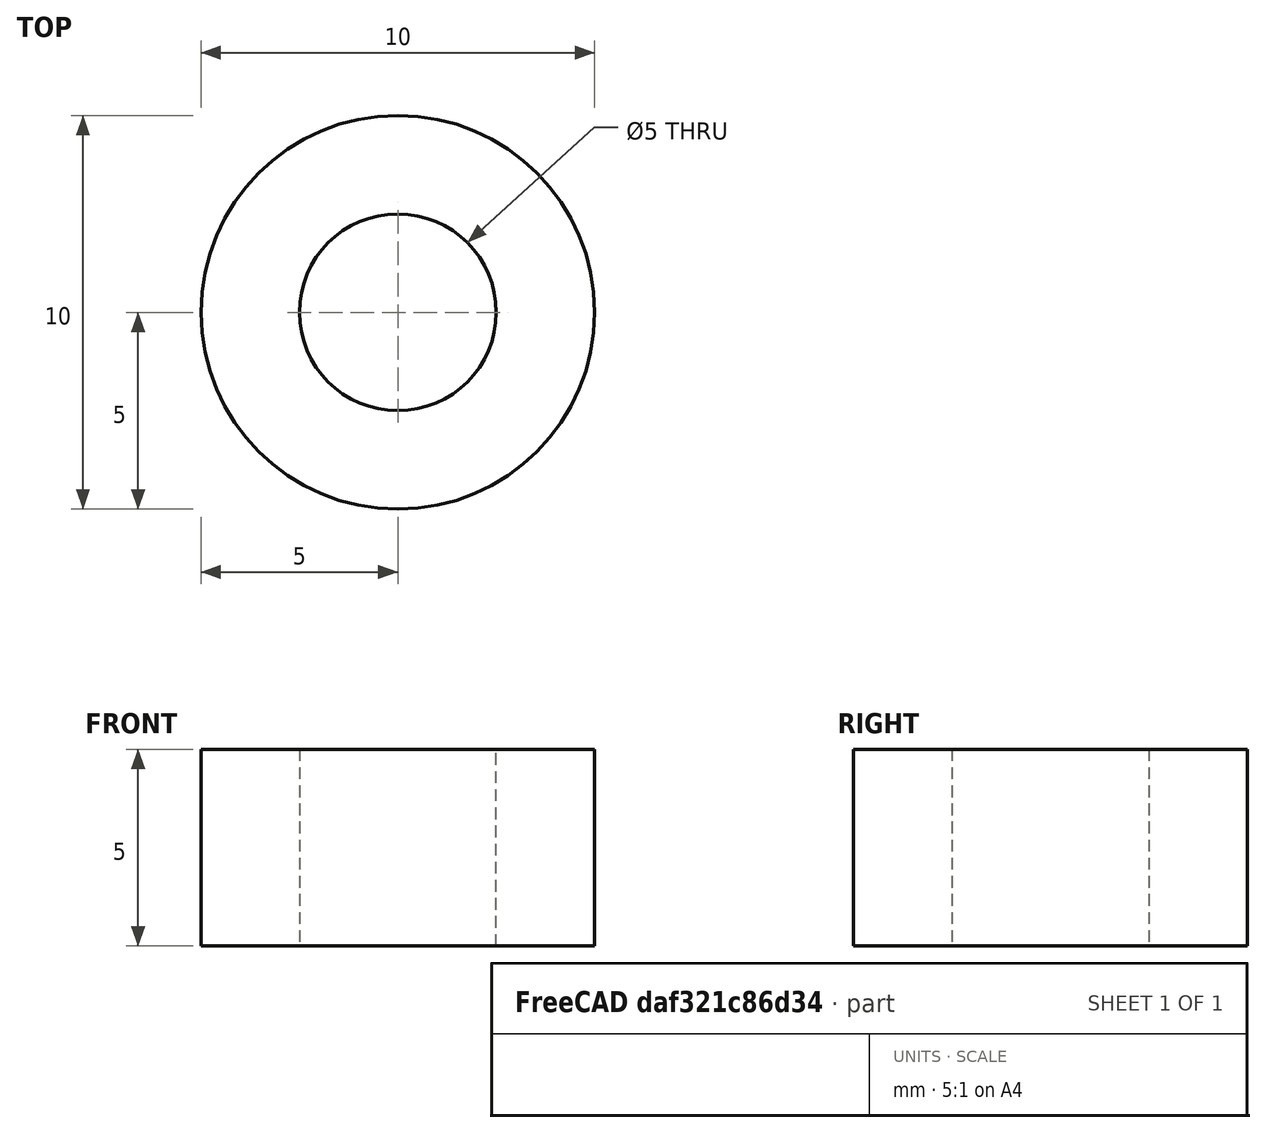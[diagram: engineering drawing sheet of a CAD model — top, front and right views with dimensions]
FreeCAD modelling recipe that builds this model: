
FCSTD DOCUMENT  (FreeCAD 1.0R39109 (Git))
Label: plate_holder
License: All rights reserved
LicenseURL: https://en.wikipedia.org/wiki/All_rights_reserved
objects: Sketcher::SketchObject×1, PartDesign::Pad×1, PartDesign::Body×1
note: 6 computed .brp shape members not serialized (recipe doc carries the construction recipe); baked Part::Feature solids carry a one-line shape summary decoded from their .brp

FEATURE [Sketcher::SketchObject] Sketch
  ArcFitTolerance = 1e-06
  AttachmentSupport = -> [XY_Plane]
  FullyConstrained = true
  MakeInternals = false
  MapMode = 5
  sketch-geometry (2):
    g0: Circle CenterX=0 CenterY=0 CenterZ=0 NormalX=0 NormalY=0 NormalZ=1 AngleXU=0 Radius=2.5
    g1: Circle CenterX=0 CenterY=0 CenterZ=0 NormalX=0 NormalY=0 NormalZ=1 AngleXU=0 Radius=5
  constraints (4):
    c: Coincident(g0,g-1)
    c: Coincident(g1,g0)
    c: Diameter(g1) = 10
    c: Diameter(g0) = 5
FEATURE [PartDesign::Pad] Pad
  Direction = (0,0,1)
  Length = 5
  Length2 = 10
  Profile = -> Sketch
  ReferenceAxis = -> Sketch [N_Axis]
  Refine = true
  Suppressed = false
  Type = 0
FEATURE [PartDesign::Body] Body  label="plate_holder"
  AllowCompound = false
  Group = -> [Sketch,Pad]
  Origin = -> Origin
  Tip = -> Pad
